# Revit family: РЗ
name_source: partatom
category: Оборудование
units: mm (PartAtom-declared; Revit-internal decimal feet)

## family parameters
Всегда вертикально = Да
Классификация = Нет
На основе рабочей плоскости = Нет
Общий = Нет
При загрузке вырезать с полостями = Нет
Размер круглого соединителя = Использовать диаметр
Тип детали = Нормальный
Точка принадлежности помещению = Нет

## types (9) — shared parameters
00_20_Manufacturer = Вентс
00_20_Name = Решітка захисна
Casing Material = Сталь, гальванизированная
Grid Material = Сетка, сталь, гальванизированная
Load Classification = HVAC
Maintenance zone material = <По категории>
URL = https://vents.ua
W = 17 мм
t = 1 мм
Изготовитель = Вентс
zero-valued in all types: Отметка по умолчанию

## per-type parameters (varying)
| type | H | H1 | L | L1 | O | h | Вага |
| РЗ 300х300 | 340 мм | 300 мм | 340 мм | 300 мм | 10 мм | 170 мм | 0.75 кг |
| РЗ 550х300 | 360 мм | 300 мм | 610 мм | 550 мм | 15 мм | 180 мм | 6.50 кг |
| РЗ 400х400 | 440 мм | 400 мм | 440 мм | 400 мм | 10 мм | 220 мм | 0.99 кг |
| РЗ 500х500 | 540 мм | 500 мм | 540 мм | 500 мм | 10 мм | 270 мм | 1.22 кг |
| РЗ 600х600 | 660 мм | 600 мм | 660 мм | 600 мм | 15 мм | 330 мм | 1.45 кг |
| РЗ 700х700 | 760 мм | 700 мм | 760 мм | 700 мм | 15 мм | 380 мм | 1.59 кг |
| РЗ 800х800 | 860 мм | 800 мм | 860 мм | 800 мм | 15 мм | 430 мм | 1.78 кг |
| РЗ 900х900 | 960 мм | 900 мм | 960 мм | 900 мм | 15 мм | 480 мм | 1.98 кг |
| РЗ 1000х1000 | 1060 мм | 1000 мм | 1060 мм | 1000 мм | 15 мм | 530 мм | 2.21 кг |

note: column(s) folded — value = type name in every type: 00_20_Type
